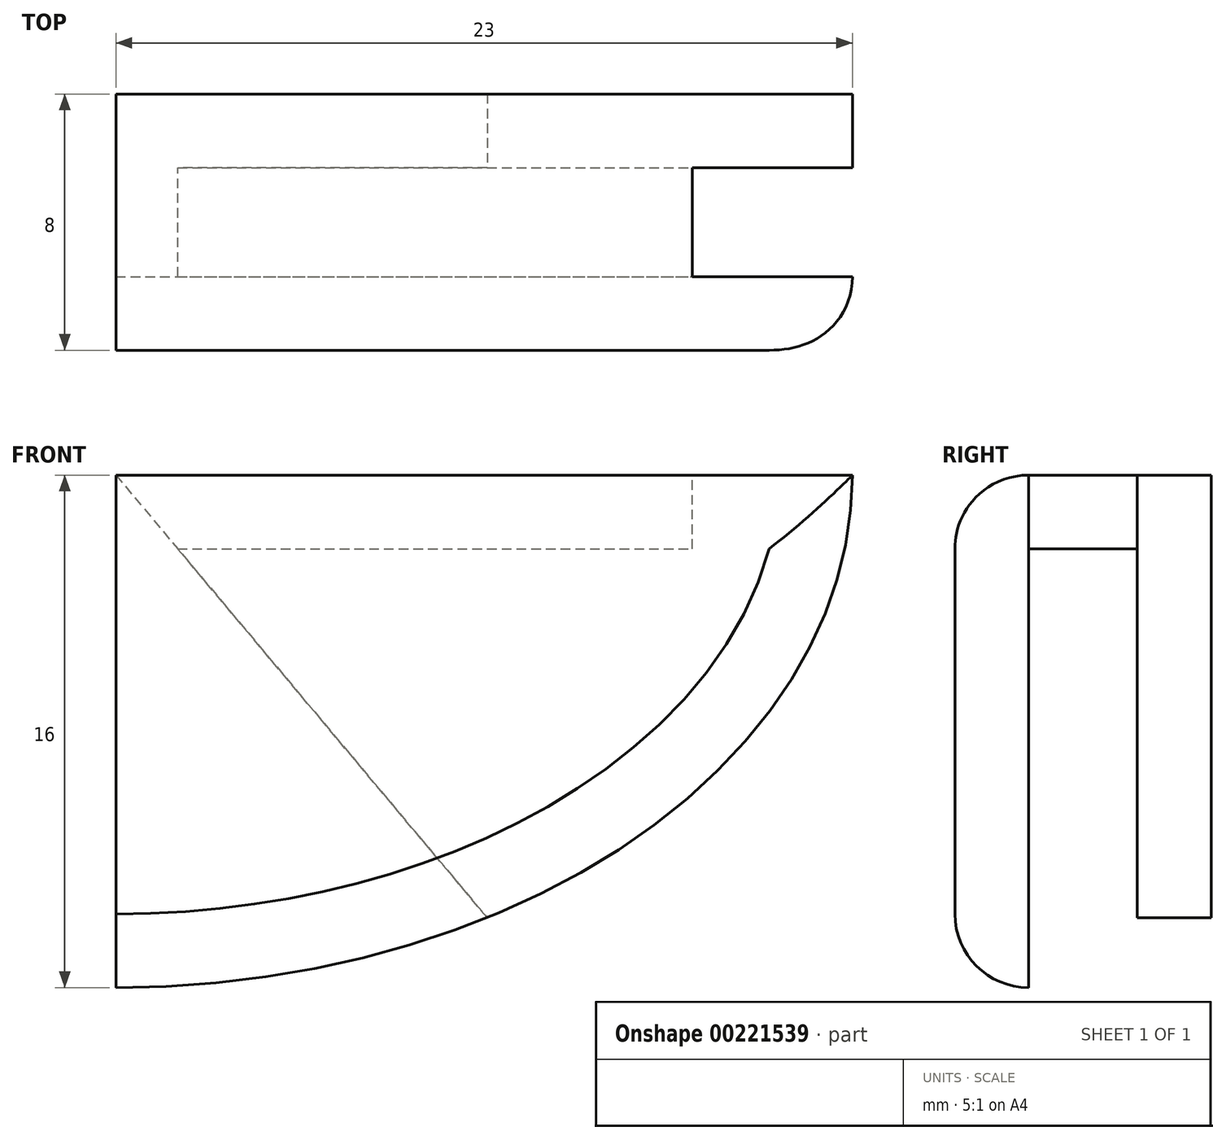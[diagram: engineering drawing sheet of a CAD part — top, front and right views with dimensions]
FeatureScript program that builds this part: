
annotation { "Feature Type Name" : "Feature", "Feature Type Description" : "" }
export const myFeature = defineFeature(function(context is Context, id is Id, definition is map)
    precondition{}
    {
        {
            var Q0;
            Q0=qCreatedBy(makeId("Front.planeOp"),FACE);
            var sketch = newSketch(context, id + "F0", { "sketchPlane" : qUnion([Q0])});
            skEllipse(sketch, "E0", {"center": v(0, 0) * mm, "majorRadius": 23 * mm, "minorRadius": 16 * mm, "majorAxis": v(-1, 0)});
            skLineSegment(sketch, "E1", {"start": v(-23, 0) * mm, "end": v(0, 0) * mm});
            skLineSegment(sketch, "E2", {"start": v(0, -16) * mm, "end": v(0, 0) * mm});
            skLineSegment(sketch, "E3", {"start": v(0, -2.3) * mm, "end": v(-22.76, -2.3) * mm});
            skLineSegment(sketch, "E4", {"start": v(0, 0) * mm, "end": v(-11.6, -13.82) * mm});
            skLineSegment(sketch, "E5", {"start": v(-18, -2.3) * mm, "end": v(-18, 0) * mm});
            skLineSegment(sketch, "E6.MirrorCS", {"start": v(23, 0) * mm, "end": v(0, 0) * mm});
            skLineSegment(sketch, "E7.MirrorCS", {"start": v(18, -2.3) * mm, "end": v(18, 0) * mm});
            skLineSegment(sketch, "E8.MirrorCS", {"start": v(0, -2.3) * mm, "end": v(22.76, -2.3) * mm});
            skLineSegment(sketch, "E9.MirrorCS", {"start": v(0, 0) * mm, "end": v(11.6, -13.82) * mm});
            skSolve(sketch);
        }
        {
            var Q0;
            {var subQ3=sQuery(id+"F0.wireOp",EDGE,"E7.MirrorCS");Q0=makeQuery(id+"F0.imprint","IMPRINT",FACE,{"disambiguationData":[TD([[makeQuery(id+"F0.imprint","IMPRINT",EDGE,{"derivedFrom":subQ3}),1.0]])]});}
            var Q1;
            {var subQ5=sQuery(id+"F0.wireOp",EDGE,"E7.MirrorCS");Q1=makeQuery(id+"F0.imprint","IMPRINT",FACE,{"disambiguationData":[TD([[makeQuery(id+"F0.imprint","IMPRINT",EDGE,{"derivedFrom":subQ5}),-1.0]])]});}
            var Q2;
            {var subQ0=sQuery(id+"F0.wireOp",EDGE,"E8.MirrorCS");var subQ1=sQuery(id+"F0.wireOp",EDGE,"E0");var subQ2=makeQuery(id+"F0.imprint","INTERSECT",VERTEX,{"derivedFrom":[subQ1,subQ0]});Q2=makeQuery(id+"F0.imprint","IMPRINT",FACE,{"disambiguationData":[TD([[makeQuery(id+"F0.imprint","IMPRINT",EDGE,{"disambiguationData":[TD([[subQ2,1.0]])],"derivedFrom":subQ1}),1.0]])]});}
            extrude(context, id + "F1", {"entities" : qUnion([Q0, Q1, Q2]), "oppositeDirection" : true, "depth" : 4 * mm});
        }
        {
            var Q0;
            {var subQ3=sQuery(id+"F0.wireOp",EDGE,"E7.MirrorCS");Q0=makeQuery(id+"F0.imprint","IMPRINT",FACE,{"disambiguationData":[TD([[makeQuery(id+"F0.imprint","IMPRINT",EDGE,{"derivedFrom":subQ3}),1.0]])]});}
            var Q1;
            {var subQ0=sQuery(id+"F0.wireOp",EDGE,"E9.MirrorCS");var subQ3=sQuery(id+"F0.wireOp",EDGE,"E8.MirrorCS");var subQ5=makeQuery(id+"F0.imprint","INTERSECT",VERTEX,{"derivedFrom":[subQ3,subQ0]});Q1=makeQuery(id+"F0.imprint","IMPRINT",FACE,{"disambiguationData":[TD([[makeQuery(id+"F0.imprint","IMPRINT",EDGE,{"disambiguationData":[TD([[subQ5,1.0]])],"derivedFrom":subQ3}),1.0]])]});}
            var Q2;
            {var subQ0=sQuery(id+"F0.wireOp",EDGE,"E2");var subQ1=sQuery(id+"F0.wireOp",EDGE,"E0");var subQ2=makeQuery(id+"F0.imprint","INTERSECT",VERTEX,{"derivedFrom":[subQ1,subQ0]});Q2=makeQuery(id+"F0.imprint","IMPRINT",FACE,{"disambiguationData":[TD([[makeQuery(id+"F0.imprint","IMPRINT",EDGE,{"disambiguationData":[TD([[subQ2,-1.0]])],"derivedFrom":subQ1}),1.0]])]});}
            var Q3;
            {var subQ0=sQuery(id+"F0.wireOp",EDGE,"E8.MirrorCS");var subQ1=sQuery(id+"F0.wireOp",EDGE,"E0");var subQ2=makeQuery(id+"F0.imprint","INTERSECT",VERTEX,{"derivedFrom":[subQ1,subQ0]});Q3=makeQuery(id+"F0.imprint","IMPRINT",FACE,{"disambiguationData":[TD([[makeQuery(id+"F0.imprint","IMPRINT",EDGE,{"disambiguationData":[TD([[subQ2,1.0]])],"derivedFrom":subQ1}),1.0]])]});}
            var Q4;
            {var subQ5=sQuery(id+"F0.wireOp",EDGE,"E7.MirrorCS");Q4=makeQuery(id+"F0.imprint","IMPRINT",FACE,{"disambiguationData":[TD([[makeQuery(id+"F0.imprint","IMPRINT",EDGE,{"derivedFrom":subQ5}),-1.0]])]});}
            extrude(context, id + "F2", {"entities" : qUnion([Q0, Q1, Q2, Q3, Q4]), "operationType" : NewBodyOperationType.ADD, "depth" : 4 * mm});
        }
        {
            var Q0;
            {var subQ0=sQuery(id+"F0.wireOp",EDGE,"E9.MirrorCS");var subQ3=sQuery(id+"F0.wireOp",EDGE,"E8.MirrorCS");var subQ5=makeQuery(id+"F0.imprint","INTERSECT",VERTEX,{"derivedFrom":[subQ3,subQ0]});Q0=makeQuery(id+"F0.imprint","IMPRINT",FACE,{"disambiguationData":[TD([[makeQuery(id+"F0.imprint","IMPRINT",EDGE,{"disambiguationData":[TD([[subQ5,1.0]])],"derivedFrom":subQ3}),1.0]])]});}
            var Q1;
            {var subQ0=sQuery(id+"F0.wireOp",EDGE,"E2");var subQ1=sQuery(id+"F0.wireOp",EDGE,"E0");var subQ2=makeQuery(id+"F0.imprint","INTERSECT",VERTEX,{"derivedFrom":[subQ1,subQ0]});Q1=makeQuery(id+"F0.imprint","IMPRINT",FACE,{"disambiguationData":[TD([[makeQuery(id+"F0.imprint","IMPRINT",EDGE,{"disambiguationData":[TD([[subQ2,-1.0]])],"derivedFrom":subQ1}),1.0]])]});}
            var Q2;
            {var subQ0=sQuery(id+"F0.wireOp",EDGE,"E8.MirrorCS");var subQ1=sQuery(id+"F0.wireOp",EDGE,"E0");var subQ2=makeQuery(id+"F0.imprint","INTERSECT",VERTEX,{"derivedFrom":[subQ1,subQ0]});Q2=makeQuery(id+"F0.imprint","IMPRINT",FACE,{"disambiguationData":[TD([[makeQuery(id+"F0.imprint","IMPRINT",EDGE,{"disambiguationData":[TD([[subQ2,1.0]])],"derivedFrom":subQ1}),1.0]])]});}
            var Q3;
            {var subQ5=sQuery(id+"F0.wireOp",EDGE,"E7.MirrorCS");Q3=makeQuery(id+"F0.imprint","IMPRINT",FACE,{"disambiguationData":[TD([[makeQuery(id+"F0.imprint","IMPRINT",EDGE,{"derivedFrom":subQ5}),-1.0]])]});}
            extrude(context, id + "F3", {"entities" : qUnion([Q0, Q1, Q2, Q3]), "operationType" : NewBodyOperationType.REMOVE, "endBound" : BoundingType.SYMMETRIC, "depth" : 3.4 * mm});
        }
        {
            var Q0;
            Q0=makeQuery(id+"F2.opExtrude","CAP_EDGE",EDGE,{"disambiguationData":[OSD([sQuery(id+"F0.wireOp",EDGE,"E6.MirrorCS")])],"isStart":false});
            var Q1;
            Q1=makeQuery(id+"F2.opExtrude","CAP_EDGE",EDGE,{"disambiguationData":[OSD([sQuery(id+"F0.wireOp",EDGE,"E0")])],"isStart":false});
            fillet(context, id + "F4", {"entities" : qUnion([Q0, Q1]), "radius" : 2.3 * mm, "tangentPropagation" : true, "allowEdgeOverflow" : false});
        }
    });
